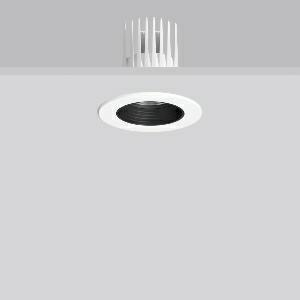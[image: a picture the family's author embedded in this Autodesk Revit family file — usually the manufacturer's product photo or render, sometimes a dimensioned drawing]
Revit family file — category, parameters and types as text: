
# Revit family: heledon_mini_e_901745_002_76_516f
name_source: partatom
category: Lighting Fixtures
units: mm (PartAtom-declared; Revit-internal decimal feet)

## family parameters
Cut with Voids When Loaded = No
Host = Face
Light Source = No
Part Type = Normal
Room Calculation Point = No
Round Connector Dimension = Use Diameter
Shared = No

## types (1)
- HELEDON mini E (1 x LED Modul 930, 2000 lm, 3000)
    Apparent Load = 20 VA
    Approval mark = CE
    CIE Flux Codes = 98 100 100 100 100
    Color Rendering = 90
    Color Temperature = 3000
    Default Elevation = 1800 mm
    Description = Series: HELEDON mini
Round recessed downlight. Housing: die-cast aluminium, powder-coated. Black plastic ring and recessed LED to prevent glare from the side. Optical assembly with lens made of plastic (polycarbonate) for the best homogeneous light distribution - can be changed without tools. Best colour rendering index Ra>90. Suitable for Recessed ceiling mounting. Installation without tools thanks to spring fastening system. Including separate LED converter with connecting cable 600 mm.High quality converter without flickering and stroboscopic effect. Through-wiring box (5 pole) available as accessory. The following accessories can be mounted without use of tools: interchangeable lenses, decorative glasses, honeycomb louvre, clear and frosted diffusers, white interchangeable plastic ring. 
Colour: traffic white, matt (RAL 9016)
Diameter: 124 mm
Height: 3 mm
Cut-out diameter: 114 mm
Recess height: 170 mm
Luminaire: recess height: 120 mm
Lamp: LED
Socket: without socket
Colour temperature: 3000K
Colour rendering index (CRI): 92
System power: 20 W
Rated luminous flux: 2000 lm
Luminous efficiency: 100 lm/W
Control gear: Converter, dimmable, DALI
Protection class: II
Type of protection: IP 20
    Height = 0 mm  [stored 0 ft]
    Lamp = 1 x LED Modul 930
    Lamp Light Flux = 2000 lm
    Lamp count = 1
    Length = 124 mm  [stored 0.406824 ft]
    Lifetime = 50000 h
    Luminous efficacy = 100 lm/W
    Manufacturer = RZB
    ModVariant = No
    Model = 901745.002.76
    Mounting Place = Ceiling
    Mounting Type = Recessed
    Number of Poles = 1
    OnlyDefault = Yes
    Power Factor = 1
    Product Name = HELEDON mini E
    Product group = Recessed downlights
    ProductGroupID = 402
    Protection Class = Protection class II
    Protection Degree = IP 20
    RLX_Detail_Level = 1
    RLX_Emergency_Light_Flux = 0 lm
    RLX_Emergency_Type = 0
    RLX_Emergency_Type_DB = No
    RlxData = <blob elided: 127589 chars, md5=03f449c4>
    Socket = socket
    Standby Power = 0 W
    System Light Flux = 2000 lm
    System Power = 20 W
    Type Comments = Product without accessories
    Type Image = 901656.002.jpg
    URL = http://relux.com
    VarID = ---
    Voltage = 230 V
    Voltage Range = 220-240 V
    Weight = 0.00 kg
    Width = 0 mm  [stored 0 ft]

note: [stored X ft] marks values corroborated as IEEE doubles in the binary element streams (Revit-internal decimal feet)

## geometry (parser evidence)
native form markers: Blend x4, Sweep x11
no freeform markers — native parametric forms only
